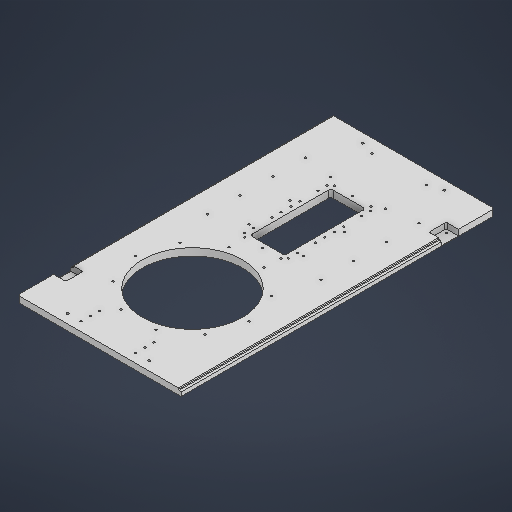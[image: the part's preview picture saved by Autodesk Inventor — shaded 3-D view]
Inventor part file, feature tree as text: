
AUTODESK INVENTOR PART (.ipt)
format: ipt  version: 2025 (Build 290162000, 162)  size: 483,328 bytes
history: native  units: in
note: dims shown in document units (in); Inventor stores cm internally (conversion verified against a paired STEP export)
features: sketch x16, extrude x5, hole x5, chamfer x5, plane x2, fillet x2
ambient origin geometry x8: Origin, YZ Plane, XZ Plane, XY Plane, X Axis, Y Axis, Z Axis, Center Point
bodies: Solid1 (feature_tree)
feature tree (35):
  extrude  "Extrusion1"  Depth=27.1654in
  sketch  "Sketch2"  dims[d5=8.6614in d6=0.0in d7=0.0in]
  extrude  "Extrusion2"  Depth=0.625in
  plane  "Work Plane1"
  hole  "Hole3"  [1 undecoded]
  sketch  "Sketch7"  dims[d69=0.1575in d70=3.937in d72=360.0deg]
  plane  "Work Plane2"
  hole  "Hole4"  [1 undecoded]
  sketch  "Sketch9"  dims[d82=1.063in]
  fillet  "Fillet2"  Radius=7.0625in
  chamfer  "Chamfer1"  Distance=3.937in Angle=360.0deg
  chamfer  "Chamfer2"  Distance=3.1102in
  extrude  "Extrusion7"  Depth=0.1969in
  extrude  "Extrusion8"  Depth=0.3937in TaperAngle=45.0deg
  chamfer  "Chamfer3"  Distance=0.0984in Angle=45.0deg
  chamfer  "Chamfer4"  Distance=0.1181in
  hole  "Hole5"  [1 undecoded]
  chamfer  "Chamfer5"  Distance=0.4951in
  hole  "Hole6"  [1 undecoded]
  sketch  "Sketch15"  dims[d86=3.1102in d87=3.1102in d88=0.1969in d89=0.0984in d90=0.0787in d91=45.0deg d92=0.0984in d93=0.0787in d94=45.0deg d95=0.1181in d96=0.1181in d97=0.4951in d98=0.0in d99=0.2362in d100=0.2362in d101=0.122in d102=0.0in d103=0.0787in d104=0.1378in d105=45.0deg d106=0.1378in d107=0.0787in d108=45.0deg d109=0.748in d110=0.315in d111=0.8661in d112=0.748in d113=0.1299in d114=0.1299in d115=0.1299in d116=0.1299in d118=0.315in d119=0.8661in d120=0.748in d121=0.748in d122=0.1276in d123=0.315in d124=0.1575in d125=0.0787in d126=90.0deg d127=0.315in d128=0.8108in d129=0.0138in d130=0.0787in d131=45.0deg d146=3.9469in d147=0.7874in d148=0.3937in d149=0.1575in d150=3.937in d152=1.1811in d153=0.3937in d155=0.3937in d157=0.1575in d158=1.1811in d160=0.7874in d161=0.3937in d163=0.3937in d165=9.8425in d166=0.1575in d167=2.9528in d168=1.1811in d169=3.1496in d171=1.4173in d172=0.3937in d174=0.3937in d176=0.1628in d177=0.3937in d178=0.1575in d179=0.0787in d180=90.0deg d181=0.3937in d182=0.8108in d191=3.0in d192=7.0in d193=6.4961in d194=0.8312in d195=0.0in d196=0.1969in d197=0.3937in d198=0.1969in d199=1.9685in d201=0.7874in d202=0.3937in d204=0.3937in d206=0.3189in d207=0.1969in d208=0.3189in d209=1.9685in d211=0.7874in d212=0.3937in d214=0.3937in d216=0.1628in d217=0.3937in d218=0.1575in d219=0.0787in d220=90.0deg d221=0.3937in d222=0.8108in d26=0.0394in d27=0.0394in d28=0.0394in d29=0.0059in d30=0.0098in d31=0.0148in d32=0.5635in d33=0.0295in d34=0.8108in d35=0.0025in d36=0.0295in d37=0.0148in d66=0.0197in d67=0.0344in]
  extrude  "Extrusion11"  Depth=0.2362in
  fillet  "Fillet3"  Radius=0.122in
  hole  "Hole7"  [1 undecoded]
  sketch  "Sketch1"  dims[d0=14.1732in d1=27.1654in]
  sketch  "Sketch6"  dims[d68=9.8425in]
  sketch  "Sketch8"  dims[d74=0.1628in d75=0.3937in d76=0.1575in d77=0.0787in d78=90.0deg d79=0.3937in d80=0.8108in]
  sketch  "Sketch Circular Pattern4"  dims[d57=0.1936in d58=0.1969in d59=0.1575in d60=0.0787in d61=90.0deg d62=0.1969in d63=0.8108in]
  sketch  "Sketch10"  dims[d83=1.063in]
  sketch  "Sketch11"  dims[d84=1.4961in]
  sketch  "Sketch12"  dims[d85=1.4961in]
  sketch  "Sketch Rectangular Pattern1"  dims[d2=0.625in d3=0.0in d4=8.0709in]
  sketch  "Sketch Rectangular Pattern2"  dims[d8=10.6299in d50=5.9055in d55=7.0625in]
  sketch  "Sketch Rectangular Pattern3"  dims[d56=25.5906in]
  sketch  "Sketch Rectangular Pattern4"  dims[d64=10.3543in]
  sketch  "Sketch Rectangular Pattern5"  dims[d65=10.6299in]
note: 5 required parameter values undecoded (feature->parameter linkage not recoverable at this tier; creation-order binding heuristic only, values carry confidence <= 0.55)
